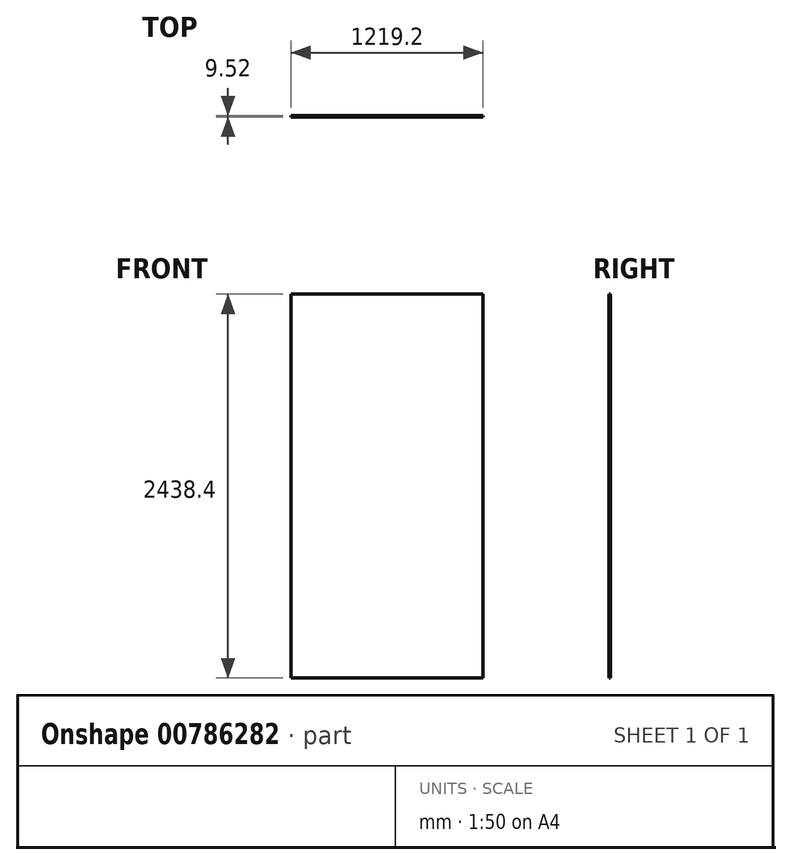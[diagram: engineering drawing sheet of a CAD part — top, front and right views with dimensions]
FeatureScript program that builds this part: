
annotation { "Feature Type Name" : "Feature", "Feature Type Description" : "" }
export const myFeature = defineFeature(function(context is Context, id is Id, definition is map)
    precondition{}
    {
        {
            var Q0;
            Q0=qCreatedBy(makeId("Front.planeOp"),FACE);
            var sketch = newSketch(context, id + "F0", { "sketchPlane" : qUnion([Q0])});
            skLineSegment(sketch, "E0.bottom", {"start": v(-609.6, 1219.2) * mm, "end": v(609.6, 1219.2) * mm});
            skLineSegment(sketch, "E0.top", {"start": v(-609.6, -1219.2) * mm, "end": v(609.6, -1219.2) * mm});
            skLineSegment(sketch, "E0.left", {"start": v(-609.6, 1219.2) * mm, "end": v(-609.6, -1219.2) * mm});
            skLineSegment(sketch, "E0.right", {"start": v(609.6, 1219.2) * mm, "end": v(609.6, -1219.2) * mm});
            skPoint(sketch, "E0.middle", {"position": v(0, 0) * mm});
            skSolve(sketch);
        }
        {
            var Q0;
            Q0=makeQuery(id+"F0.imprint","IMPRINT",FACE,{"disambiguationData":[TD([[makeQuery(id+"F0.imprint","IMPRINT",EDGE,{"derivedFrom":sQuery(id+"F0.wireOp",EDGE,"E0.bottom")}),-1.0]])]});
            extrude(context, id + "F1", {"entities" : qUnion([Q0]), "endBound" : BoundingType.SYMMETRIC, "depth" : 9.52 * mm, "offsetDistance" : 25.4 * mm});
        }
    });
